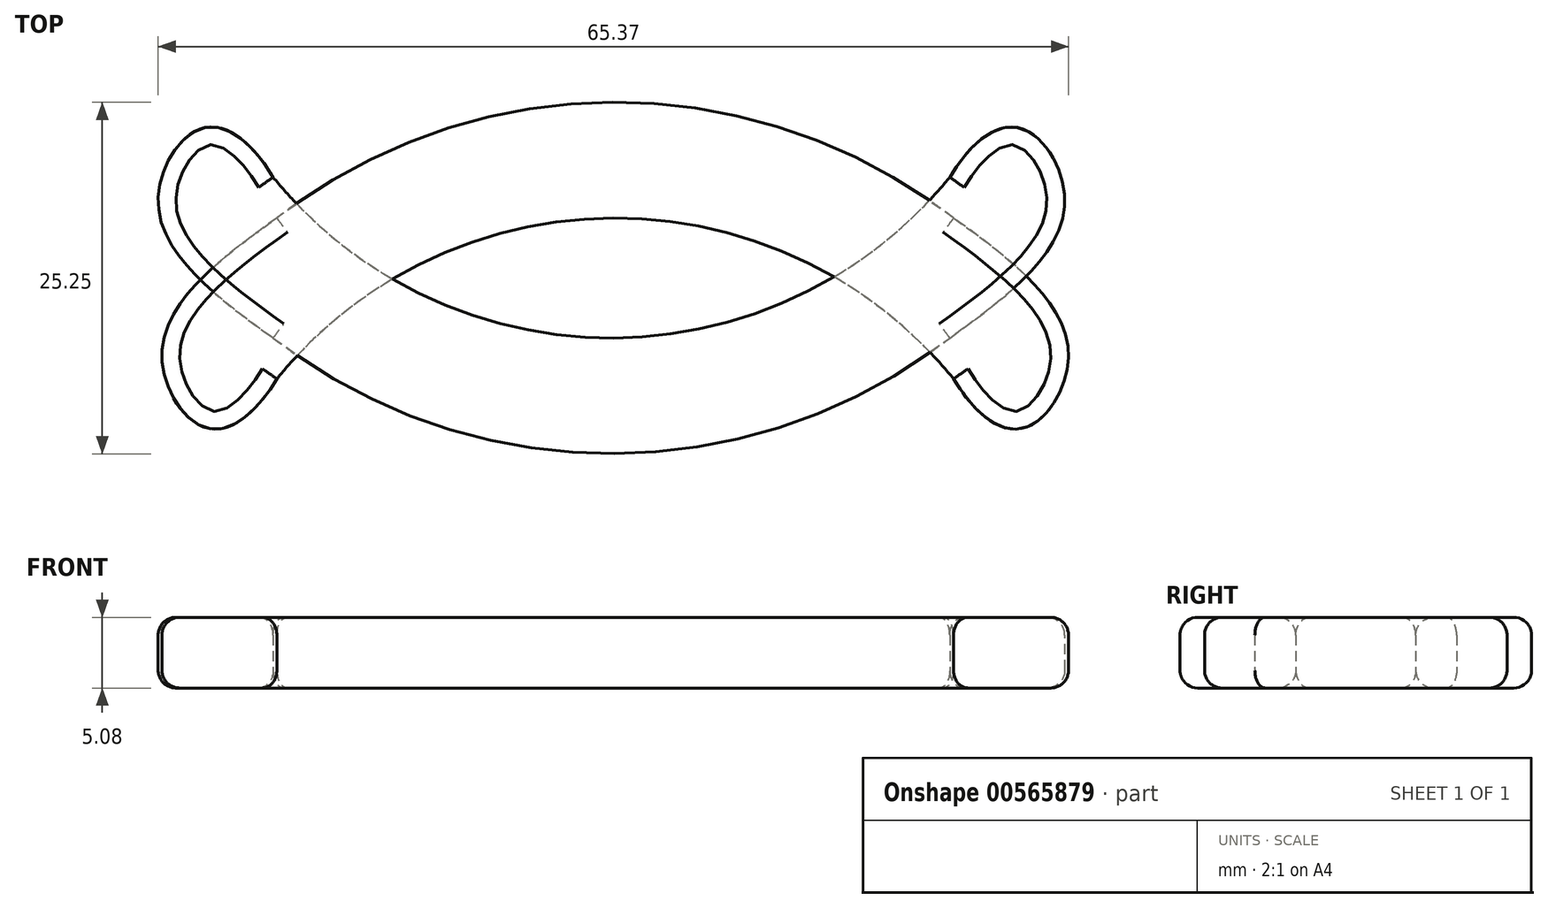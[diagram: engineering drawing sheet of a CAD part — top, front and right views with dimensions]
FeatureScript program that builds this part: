
annotation { "Feature Type Name" : "Feature", "Feature Type Description" : "" }
export const myFeature = defineFeature(function(context is Context, id is Id, definition is map)
    precondition{}
    {
        {
            var Q0;
            Q0=qCreatedBy(makeId("Top.planeOp"),FACE);
            var sketch = newSketch(context, id + "F0", { "sketchPlane" : qUnion([Q0])});
            skArc(sketch, "E0", {"start": v(0, 0) * mm, "mid": v(24.3, -11.55) * mm, "end": v(48.58, 0) * mm});
            skArc(sketch, "E1", {"start": v(0, -11.55) * mm, "mid": v(24.3, -19.87) * mm, "end": v(48.58, -11.55) * mm});
            skPoint(sketch, "E1.startSnap0", {"position": v(24.3, -11.55) * mm});
            skLineSegment(sketch, "E2", {"start": v(48.58, 0) * mm, "end": v(48.58, -11.55) * mm, "construction": true});
            skLineSegment(sketch, "E3", {"start": v(0, 0) * mm, "end": v(0, -11.55) * mm, "construction": true});
            skFitSpline(sketch, "E4", {"points": [v(48.58, 0) * mm, v(53.68, 3.52) * mm, v(56.82, -2.2) * mm, v(48.58, -11.55) * mm], "startDerivative": vector(15.54, 25.68) * mm, "endDerivative": vector(-29.86, -21.1) * mm});
            skFitSpline(sketch, "E5.MirrorCS", {"points": [v(0, 0) * mm, v(-5.1, 3.52) * mm, v(-8.23, -2.2) * mm, v(0, -11.55) * mm], "startDerivative": vector(-15.54, 25.68) * mm, "endDerivative": vector(29.86, -21.1) * mm});
            skSolve(sketch);
        }
        {
            var Q0;
            Q0=qCreatedBy(makeId("Top.planeOp"),FACE);
            var sketch = newSketch(context, id + "F1", { "sketchPlane" : qUnion([Q0])});
            skArc(sketch, "E6", {"start": v(48.85, -14.49) * mm, "mid": v(24.56, -2.94) * mm, "end": v(0.27, -14.49) * mm});
            skArc(sketch, "E7", {"start": v(48.85, -2.94) * mm, "mid": v(24.56, 5.38) * mm, "end": v(0.27, -2.94) * mm});
            skPoint(sketch, "E7.startSnap0", {"position": v(0, -3.95) * mm});
            skLineSegment(sketch, "E8", {"start": v(0.27, -14.49) * mm, "end": v(0.27, -2.94) * mm, "construction": true});
            skLineSegment(sketch, "E9", {"start": v(48.85, -14.49) * mm, "end": v(48.85, -2.94) * mm, "construction": true});
            skFitSpline(sketch, "E10", {"points": [v(0.27, -14.49) * mm, v(-4.83, -18) * mm, v(-7.97, -12.3) * mm, v(0.27, -2.94) * mm], "startDerivative": vector(-15.54, -25.68) * mm, "endDerivative": vector(29.86, 21.1) * mm});
            skFitSpline(sketch, "E11.MirrorCS", {"points": [v(48.85, -14.49) * mm, v(53.95, -18) * mm, v(57.09, -12.3) * mm, v(48.85, -2.94) * mm], "startDerivative": vector(15.54, -25.68) * mm, "endDerivative": vector(-29.86, 21.1) * mm});
            skSolve(sketch);
        }
        {
            var Q0;
            Q0 = qSketchRegion(id + "F0", true);
            var Q1;
            Q1 = qSketchRegion(id + "F1", true);
            extrude(context, id + "F2", {"entities" : qUnion([Q0, Q1]), "depth" : 5.08 * mm, "offsetDistance" : 25.4 * mm});
        }
        {
            var Q0;
            Q0=makeQuery(id+"F2.opExtrude","CAP_EDGE",EDGE,{"disambiguationData":[OSD([sQuery(id+"F0.wireOp",EDGE,"E5.MirrorCS")])],"isStart":false});
            var Q1;
            Q1=makeQuery(id+"F2.opExtrude","CAP_EDGE",EDGE,{"disambiguationData":[OSD([sQuery(id+"F0.wireOp",EDGE,"E0")])],"isStart":false});
            var Q2;
            Q2=makeQuery(id+"F2.opExtrude","CAP_EDGE",EDGE,{"disambiguationData":[OSD([sQuery(id+"F0.wireOp",EDGE,"E1")])],"isStart":false});
            var Q3;
            Q3=makeQuery(id+"F2.opExtrude","CAP_EDGE",EDGE,{"disambiguationData":[OSD([sQuery(id+"F0.wireOp",EDGE,"E4")])],"isStart":false});
            fillet(context, id + "F3", {"entities" : qUnion([Q0, Q1, Q2, Q3]), "radius" : 1.27 * mm, "tangentPropagation" : true, "allowEdgeOverflow" : false});
        }
        {
            var Q0;
            Q0=makeQuery(id+"F2.opExtrude","CAP_EDGE",EDGE,{"disambiguationData":[OSD([sQuery(id+"F1.wireOp",EDGE,"E7")])],"isStart":false});
            var Q1;
            Q1=makeQuery(id+"F2.opExtrude","CAP_FACE",FACE,{"disambiguationData":[OSD([sQuery(id+"F1.wireOp",EDGE,"E6"),sQuery(id+"F1.wireOp",EDGE,"E7"),sQuery(id+"F1.wireOp",EDGE,"E10"),sQuery(id+"F1.wireOp",EDGE,"E11.MirrorCS")])],"isStart":false});
            fillet(context, id + "F4", {"entities" : qUnion([Q0, Q1]), "radius" : 1.27 * mm, "tangentPropagation" : true, "allowEdgeOverflow" : false});
        }
        {
            var Q0;
            Q0=makeQuery(id+"F2.opExtrude","CAP_FACE",FACE,{"disambiguationData":[OSD([sQuery(id+"F0.wireOp",EDGE,"E0"),sQuery(id+"F0.wireOp",EDGE,"E1"),sQuery(id+"F0.wireOp",EDGE,"E4"),sQuery(id+"F0.wireOp",EDGE,"E5.MirrorCS")])],"isStart":true});
            fillet(context, id + "F5", {"entities" : qUnion([Q0]), "radius" : 1.27 * mm, "tangentPropagation" : true, "allowEdgeOverflow" : false});
        }
        {
            var Q0;
            Q0=makeQuery(id+"F2.opExtrude","CAP_FACE",FACE,{"disambiguationData":[OSD([sQuery(id+"F1.wireOp",EDGE,"E6"),sQuery(id+"F1.wireOp",EDGE,"E7"),sQuery(id+"F1.wireOp",EDGE,"E10"),sQuery(id+"F1.wireOp",EDGE,"E11.MirrorCS")])],"isStart":true});
            fillet(context, id + "F6", {"entities" : qUnion([Q0]), "radius" : 1.27 * mm, "tangentPropagation" : true, "allowEdgeOverflow" : false});
        }
    });
